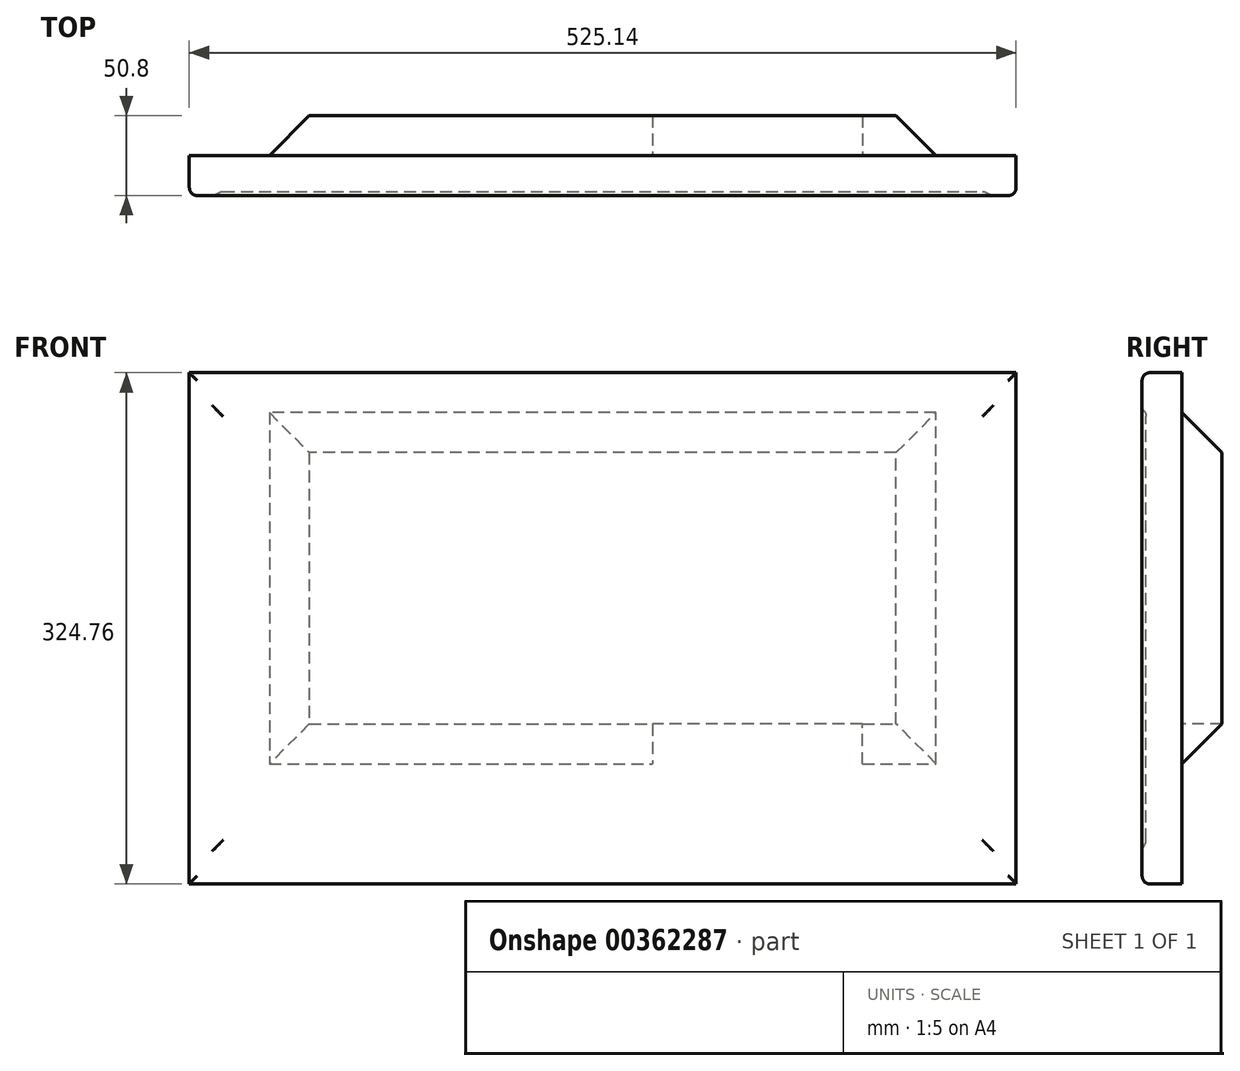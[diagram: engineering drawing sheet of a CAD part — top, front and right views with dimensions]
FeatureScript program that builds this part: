
annotation { "Feature Type Name" : "Feature", "Feature Type Description" : "" }
export const myFeature = defineFeature(function(context is Context, id is Id, definition is map)
    precondition{}
    {
        {
            var Q0;
            Q0=qCreatedBy(makeId("Front.planeOp"),FACE);
            var sketch = newSketch(context, id + "F0", { "sketchPlane" : qUnion([Q0])});
            skLineSegment(sketch, "E0.bottom", {"start": v(243.52, -136.98) * mm, "end": v(-243.52, -136.98) * mm});
            skLineSegment(sketch, "E0.top", {"start": v(243.52, 136.98) * mm, "end": v(-243.52, 136.98) * mm});
            skLineSegment(sketch, "E0.left", {"start": v(-243.52, 136.98) * mm, "end": v(-243.52, -136.98) * mm});
            skLineSegment(sketch, "E0.right", {"start": v(243.52, 136.98) * mm, "end": v(243.52, -136.98) * mm});
            skPoint(sketch, "E0.middle", {"position": v(0, 0) * mm});
            skLineSegment(sketch, "E1", {"start": v(-243.52, -136.98) * mm, "end": v(243.52, 136.98) * mm});
            skLineSegment(sketch, "E2.bottom", {"start": v(-262.57, 162.38) * mm, "end": v(262.57, 162.38) * mm});
            skLineSegment(sketch, "E2.top", {"start": v(-262.57, -162.38) * mm, "end": v(262.57, -162.38) * mm});
            skLineSegment(sketch, "E2.left", {"start": v(-262.57, 162.38) * mm, "end": v(-262.57, -162.38) * mm});
            skLineSegment(sketch, "E2.right", {"start": v(262.57, 162.38) * mm, "end": v(262.57, -162.38) * mm});
            skSolve(sketch);
        }
        {
            var Q0;
            Q0=makeQuery(id+"F0.imprint","IMPRINT",FACE,{"disambiguationData":[TD([[makeQuery(id+"F0.imprint","IMPRINT",EDGE,{"derivedFrom":sQuery(id+"F0.wireOp",EDGE,"E0.bottom")}),1.0]])]});
            extrude(context, id + "F1", {"entities" : qUnion([Q0]), "depth" : 25.4 * mm});
        }
        {
            var Q0;
            Q0=makeQuery(id+"F0.imprint","IMPRINT",FACE,{"disambiguationData":[TD([[makeQuery(id+"F0.imprint","IMPRINT",EDGE,{"derivedFrom":sQuery(id+"F0.wireOp",EDGE,"E0.top")}),1.0]])]});
            var Q1;
            Q1=makeQuery(id+"F0.imprint","IMPRINT",FACE,{"disambiguationData":[TD([[makeQuery(id+"F0.imprint","IMPRINT",EDGE,{"derivedFrom":sQuery(id+"F0.wireOp",EDGE,"E0.bottom")}),-1.0]])]});
            extrude(context, id + "F2", {"entities" : qUnion([Q0, Q1]), "operationType" : NewBodyOperationType.ADD, "depth" : 22.86 * mm});
        }
        {
            var Q0;
            Q0=makeQuery(id+"F1.opExtrude","CAP_FACE",FACE,{"disambiguationData":[OSD([sQuery(id+"F0.wireOp",EDGE,"E0.bottom"),sQuery(id+"F0.wireOp",EDGE,"E0.top"),sQuery(id+"F0.wireOp",EDGE,"E0.left"),sQuery(id+"F0.wireOp",EDGE,"E0.right"),sQuery(id+"F0.wireOp",EDGE,"E2.bottom"),sQuery(id+"F0.wireOp",EDGE,"E2.top"),sQuery(id+"F0.wireOp",EDGE,"E2.left"),sQuery(id+"F0.wireOp",EDGE,"E2.right")])],"isStart":false});
            fillet(context, id + "F3", {"entities" : qUnion([Q0]), "radius" : 5.08 * mm, "tangentPropagation" : true, "allowEdgeOverflow" : false});
        }
        {
            var Q0;
            Q0=makeQuery(id+"F2.opExtrude","CAP_FACE",FACE,{"disambiguationData":[OSD([sQuery(id+"F0.wireOp",EDGE,"E0.bottom"),sQuery(id+"F0.wireOp",EDGE,"E0.top"),sQuery(id+"F0.wireOp",EDGE,"E0.left"),sQuery(id+"F0.wireOp",EDGE,"E0.right")])],"isStart":false});
            fillet(context, id + "F4", {"entities" : qUnion([Q0]), "radius" : 5.08 * mm, "tangentPropagation" : true, "allowEdgeOverflow" : false});
        }
        {
            var Q0;
            {var subQ0=sQuery(id+"F0.wireOp",EDGE,"E0.right");var subQ1=sQuery(id+"F0.wireOp",EDGE,"E0.left");var subQ2=sQuery(id+"F0.wireOp",EDGE,"E0.top");var subQ3=sQuery(id+"F0.wireOp",EDGE,"E0.bottom");Q0=makeQuery(id+"F2.boolean.opBoolean","MERGE",FACE,{"derivedFrom":[makeQuery(id+"F1.opExtrude","CAP_FACE",FACE,{"disambiguationData":[OSD([subQ3,subQ2,subQ1,subQ0,sQuery(id+"F0.wireOp",EDGE,"E2.bottom"),sQuery(id+"F0.wireOp",EDGE,"E2.top"),sQuery(id+"F0.wireOp",EDGE,"E2.left"),sQuery(id+"F0.wireOp",EDGE,"E2.right")])],"isStart":true}),makeQuery(id+"F2.opExtrude","CAP_FACE",FACE,{"disambiguationData":[OSD([subQ3,subQ2,subQ1,subQ0])],"isStart":true})]});}
            var sketch = newSketch(context, id + "F5", { "sketchPlane" : qUnion([Q0])});
            skLineSegment(sketch, "E3.bottom", {"start": v(-211.77, -86.18) * mm, "end": v(211.77, -86.18) * mm});
            skLineSegment(sketch, "E3.top", {"start": v(-211.77, 136.98) * mm, "end": v(211.77, 136.98) * mm});
            skLineSegment(sketch, "E3.left", {"start": v(-211.77, -86.18) * mm, "end": v(-211.77, 136.98) * mm});
            skLineSegment(sketch, "E3.right", {"start": v(211.77, -86.18) * mm, "end": v(211.77, 136.98) * mm});
            skSolve(sketch);
        }
        {
            var Q0;
            Q0 = qSketchRegion(id + "F5", true);
            extrude(context, id + "F6", {"entities" : qUnion([Q0]), "operationType" : NewBodyOperationType.ADD, "depth" : 25.4 * mm, "hasDraft" : true, "draftAngle" : 45 * degree, "draftPullDirection" : true});
        }
        {
            var Q0;
            {var subQ0=sQuery(id+"F0.wireOp",EDGE,"E0.right");var subQ1=sQuery(id+"F0.wireOp",EDGE,"E0.left");var subQ2=sQuery(id+"F0.wireOp",EDGE,"E0.top");var subQ3=sQuery(id+"F0.wireOp",EDGE,"E0.bottom");Q0=makeQuery(id+"F2.boolean.opBoolean","MERGE",FACE,{"derivedFrom":[makeQuery(id+"F1.opExtrude","CAP_FACE",FACE,{"disambiguationData":[OSD([subQ3,subQ2,subQ1,subQ0,sQuery(id+"F0.wireOp",EDGE,"E2.bottom"),sQuery(id+"F0.wireOp",EDGE,"E2.top"),sQuery(id+"F0.wireOp",EDGE,"E2.left"),sQuery(id+"F0.wireOp",EDGE,"E2.right")])],"isStart":true}),makeQuery(id+"F2.opExtrude","CAP_FACE",FACE,{"disambiguationData":[OSD([subQ3,subQ2,subQ1,subQ0])],"isStart":true})]});}
            var sketch = newSketch(context, id + "F7", { "sketchPlane" : qUnion([Q0])});
            skLineSegment(sketch, "E4.bottom", {"start": v(-164.97, -86.18) * mm, "end": v(-31.46, -86.18) * mm});
            skLineSegment(sketch, "E4.top", {"start": v(-164.97, -60.78) * mm, "end": v(-31.46, -60.78) * mm});
            skLineSegment(sketch, "E4.left", {"start": v(-164.97, -86.18) * mm, "end": v(-164.97, -60.78) * mm});
            skLineSegment(sketch, "E4.right", {"start": v(-31.46, -86.18) * mm, "end": v(-31.46, -60.78) * mm});
            skSolve(sketch);
        }
        {
            var Q0;
            Q0 = qSketchRegion(id + "F7", true);
            extrude(context, id + "F8", {"entities" : qUnion([Q0]), "operationType" : NewBodyOperationType.REMOVE, "depth" : 25.4 * mm});
        }
    });
